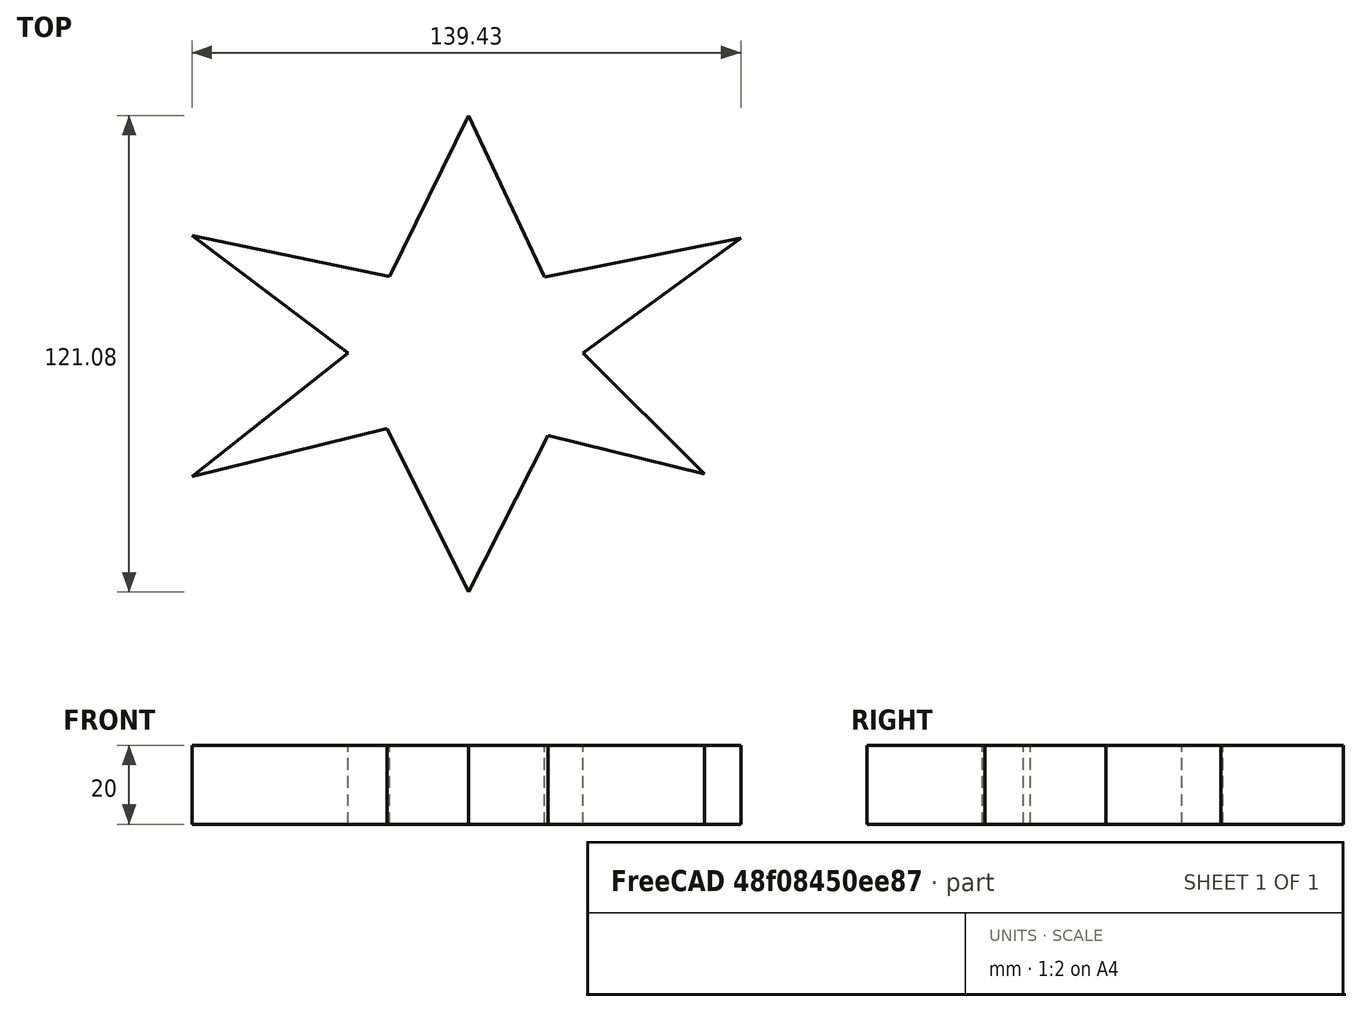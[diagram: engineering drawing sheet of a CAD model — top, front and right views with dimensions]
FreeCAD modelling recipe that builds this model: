
FCSTD DOCUMENT  (FreeCAD 0.21R33694 (Git))
Label: OJT1_T016P01_estrella
License: All rights reserved
LicenseURL: http://en.wikipedia.org/wiki/All_rights_reserved
objects: Sketcher::SketchObject×1, PartDesign::Pad×1, PartDesign::Body×1
note: 4 computed .brp shape members not serialized (recipe doc carries the construction recipe); baked Part::Feature solids carry a one-line shape summary decoded from their .brp

FEATURE [Sketcher::SketchObject] Sketch
  FullyConstrained = false
  MapMode = 5
  Support = -> [XY_Plane]
  sketch-geometry (12):
    g0: LineSegment StartX=0 StartY=60.4014 StartZ=0 EndX=19.3811 EndY=19.3811 EndZ=0
    g1: LineSegment StartX=19.3811 StartY=19.3811 StartZ=0 EndX=69.2167 EndY=29.2137 EndZ=0
    g2: LineSegment StartX=69.2167 StartY=29.2137 StartZ=0 EndX=29.1292 EndY=0 EndZ=0
    g3: LineSegment StartX=29.1292 StartY=0 StartZ=0 EndX=60.0439 EndY=-30.7157 EndZ=0
    g4: LineSegment StartX=60.0439 StartY=-30.7157 StartZ=0 EndX=20.2948 EndY=-20.9313 EndZ=0
    g5: LineSegment StartX=20.2948 StartY=-20.9313 StartZ=0 EndX=0 EndY=-60.6804 EndZ=0
    g6: LineSegment StartX=0 StartY=-60.6804 StartZ=0 EndX=-20.6773 EndY=-19.0968 EndZ=0
    g7: LineSegment StartX=-20.6773 StartY=-19.0968 StartZ=0 EndX=-70.2108 EndY=-31.3272 EndZ=0
    g8: LineSegment StartX=-70.2108 StartY=-31.3272 StartZ=0 EndX=-30.5595 EndY=3.6e-15 EndZ=0
    g9: LineSegment StartX=-30.5595 StartY=3.6e-15 StartZ=0 EndX=-70.2108 EndY=29.8252 EndZ=0
    g10: LineSegment StartX=-70.2108 StartY=29.8252 StartZ=0 EndX=-20.0658 EndY=19.4293 EndZ=0
    g11: LineSegment StartX=-20.0658 StartY=19.4293 StartZ=0 EndX=0 EndY=60.4014 EndZ=0
  constraints (16):
    c: PointOnObject(g0,g-2)
    c: Coincident(g0,g1)
    c: Coincident(g1,g2)
    c: PointOnObject(g2,g-1)
    c: Coincident(g2,g3)
    c: Coincident(g3,g4)
    c: Coincident(g4,g5)
    c: PointOnObject(g5,g-2)
    c: Coincident(g5,g6)
    c: Coincident(g6,g7)
    c: Coincident(g7,g8)
    c: PointOnObject(g8,g-1)
    c: Coincident(g8,g9)
    c: Coincident(g9,g10)
    c: Coincident(g10,g11)
    c: Coincident(g11,g0)
FEATURE [PartDesign::Pad] Pad  label="boceto_estrella"
  Direction = (0,0,1)
  Length = 20
  Length2 = 10
  Profile = -> Sketch
  ReferenceAxis = -> Sketch [N_Axis]
  Type = 0
FEATURE [PartDesign::Body] Body  label="ESTRELLA"
  Group = -> [Sketch,Pad]
  Origin = -> Origin
  Tip = -> Pad
